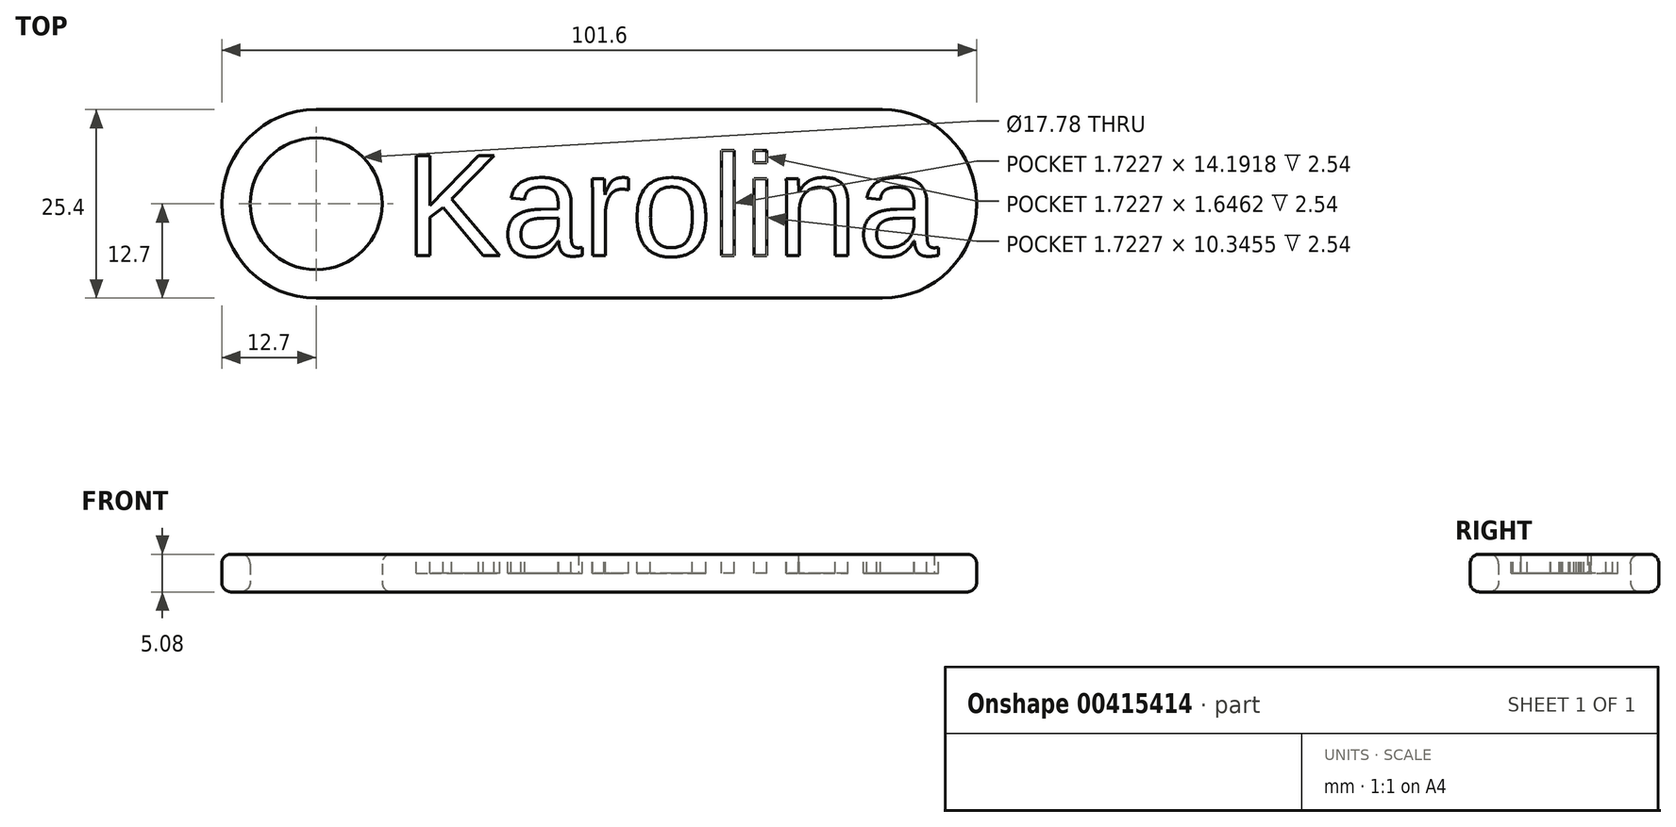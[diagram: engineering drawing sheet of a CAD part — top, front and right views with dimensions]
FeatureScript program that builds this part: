
annotation { "Feature Type Name" : "Feature", "Feature Type Description" : "" }
export const myFeature = defineFeature(function(context is Context, id is Id, definition is map)
    precondition{}
    {
        {
            var Q0;
            Q0=qCreatedBy(makeId("Top.planeOp"),FACE);
            var sketch = newSketch(context, id + "F0", { "sketchPlane" : qUnion([Q0])});
            skLineSegment(sketch, "E0.bottom", {"start": v(38.1, -12.7) * mm, "end": v(-38.1, -12.7) * mm});
            skLineSegment(sketch, "E0.top", {"start": v(38.1, 12.7) * mm, "end": v(-38.1, 12.7) * mm});
            skPoint(sketch, "E0.middle", {"position": v(0, 0) * mm});
            skArc(sketch, "E1", {"start": v(38.1, -12.7) * mm, "mid": v(50.8, 0) * mm, "end": v(38.1, 12.7) * mm});
            skArc(sketch, "E2", {"start": v(-38.1, 12.7) * mm, "mid": v(-50.8, 0) * mm, "end": v(-38.1, -12.7) * mm});
            skCircle(sketch, "E3", {"center": v(-38.1, 0) * mm, "radius": 8.9 * mm});
            skSolve(sketch);
        }
        {
            var Q0;
            Q0=makeQuery(id+"F0.imprint","IMPRINT",FACE,{"disambiguationData":[TD([[makeQuery(id+"F0.imprint","IMPRINT",EDGE,{"derivedFrom":sQuery(id+"F0.wireOp",EDGE,"E0.bottom")}),-1.0]])]});
            extrude(context, id + "F1", {"entities" : qUnion([Q0]), "depth" : 5.08 * mm});
        }
        {
            var Q0;
            Q0=makeQuery(id+"F1.opExtrude","CAP_FACE",FACE,{"disambiguationData":[OSD([sQuery(id+"F0.wireOp",EDGE,"E0.bottom"),sQuery(id+"F0.wireOp",EDGE,"E0.top"),sQuery(id+"F0.wireOp",EDGE,"E1"),sQuery(id+"F0.wireOp",EDGE,"E2"),sQuery(id+"F0.wireOp",EDGE,"E3")])],"isStart":false});
            var sketch = newSketch(context, id + "F2", { "sketchPlane" : qUnion([Q0])});
            skText(sketch, "E4", { "text": "Karolina", "fontName": "Arimo-Regular.ttf"});
            const initialGuessF2  = {"E4": [-0.0262, -0.00699, 1, 0, 0.0141]};
            skSetInitialGuess(sketch, initialGuessF2);
            skSolve(sketch);
        }
        {
            var Q0;
            Q0=qSketchRegion(id+"F2",true);
            extrude(context, id + "F3", {"entities" : qUnion([Q0]), "operationType" : NewBodyOperationType.REMOVE, "oppositeDirection" : true, "depth" : 2.54 * mm});
        }
        {
            var Q0;
            Q0=makeQuery(id+"F1.opExtrude","CAP_EDGE",EDGE,{"disambiguationData":[OSD([sQuery(id+"F0.wireOp",EDGE,"E2")])],"isStart":false});
            var Q1;
            Q1=makeQuery(id+"F1.opExtrude","CAP_FACE",FACE,{"disambiguationData":[OSD([sQuery(id+"F0.wireOp",EDGE,"E0.bottom"),sQuery(id+"F0.wireOp",EDGE,"E0.top"),sQuery(id+"F0.wireOp",EDGE,"E1"),sQuery(id+"F0.wireOp",EDGE,"E2"),sQuery(id+"F0.wireOp",EDGE,"E3")])],"isStart":true});
            var Q2;
            Q2=makeQuery(id+"F1.opExtrude","CAP_EDGE",EDGE,{"disambiguationData":[OSD([sQuery(id+"F0.wireOp",EDGE,"E3")])],"isStart":false});
            fillet(context, id + "F4", {"entities" : qUnion([Q0, Q1, Q2]), "radius" : 1.27 * mm, "tangentPropagation" : true, "allowEdgeOverflow" : false});
        }
    });
